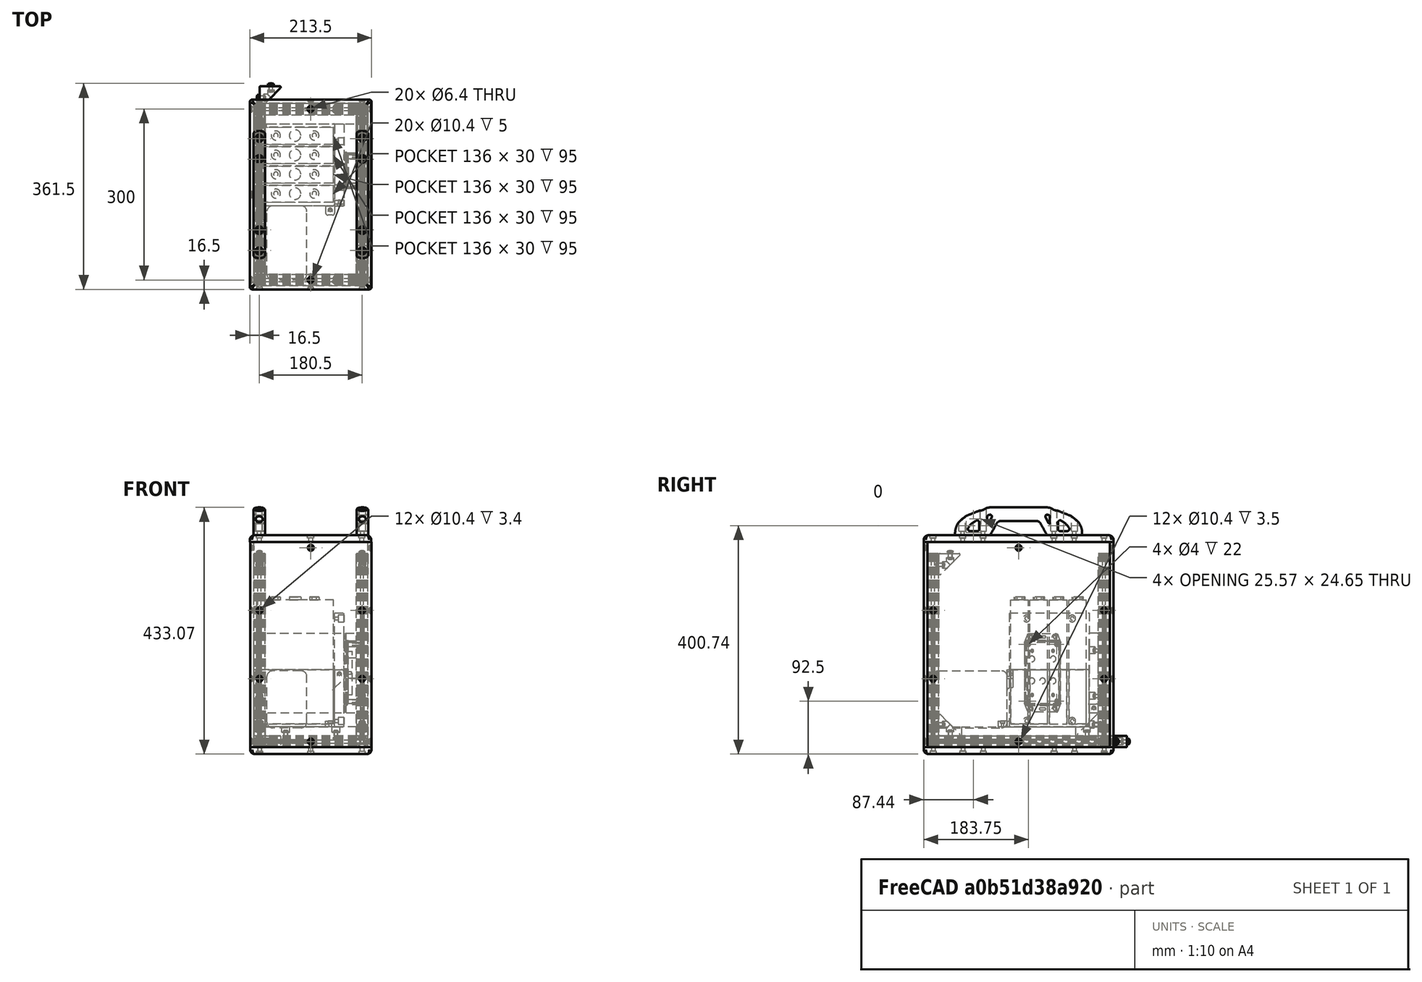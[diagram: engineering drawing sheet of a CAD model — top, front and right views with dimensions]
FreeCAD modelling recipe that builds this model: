
FCSTD DOCUMENT  (FreeCAD 0.17R9796 (Git))
Label: UPKframeNG2h
License: All rights reserved
LicenseURL: http://en.wikipedia.org/wiki/All_rights_reserved
objects: Part::Feature×72, Part::FeaturePython×24, Part::Compound×12, App::FeaturePython×8, App::Part×6, Part::Cylinder×5, Part::Box×4, Part::Cut×4, PartDesign::Body×2, PartDesign::Pocket×1, Part::Fillet×1, Part::MultiFuse×1
note: 127 computed .brp shape members not serialized (recipe doc carries the construction recipe); baked Part::Feature solids carry a one-line shape summary decoded from their .brp

FEATURE [Part::Feature] Pocket003001  label="tslot32con"
  Placement = pos=(0,10,10) rot=(1,0,0;1.5708rad)
  shape: bbox 20 x 320 x 20 mm, 150 faces (baked)
FEATURE [Part::Feature] Pocket003002  label="tslot16"
  Placement = pos=(10,0,10) rot=(0,1,0;1.5708rad)
  shape: bbox 160 x 20 x 20 mm, 94 faces (baked)
FEATURE [Part::Feature] Pocket003006  label="tslot16_001"
  Placement = pos=(10,-300,10) rot=(0,1,0;1.5708rad)
  shape: bbox 160 x 20 x 20 mm, 94 faces (baked)
FEATURE [Part::Feature] Pocket003007  label="tslot32con_001"
  Placement = pos=(180,-310,10) rot=(0,0.707107,0.707107;3.14159rad)
  shape: bbox 20 x 320 x 20 mm, 150 faces (baked)
FEATURE [Part::FeaturePython] Screw  label="M6x25-Screw"  # Fasteners workbench fastener (typed FeaturePython)
  Placement = pos=(-4,0,10) rot=(0,-1,0;1.5708rad)
  diameter = 7
  invert = false
  length = 6
  matchOuter = false
  offset = 0
  thread = false
  type = 15
FEATURE [Part::FeaturePython] Screw001  label="M6x25-Screw004"  # Fasteners workbench fastener (typed FeaturePython)
  Placement = pos=(-4,-300,10) rot=(0,-1,0;1.5708rad)
  diameter = 7
  invert = false
  length = 6
  matchOuter = false
  offset = 0
  thread = false
  type = 15
FEATURE [Part::FeaturePython] Screw002  label="M6x25-Screw005"  # Fasteners workbench fastener (typed FeaturePython)
  Placement = pos=(184,0,10) rot=(0,1,0;1.5708rad)
  diameter = 7
  invert = false
  length = 6
  matchOuter = false
  offset = 0
  thread = false
  type = 15
FEATURE [Part::FeaturePython] Screw004  label="M6x25-Screw006"  # Fasteners workbench fastener (typed FeaturePython)
  Placement = pos=(184,-300,10) rot=(0,1,0;1.5708rad)
  diameter = 7
  invert = false
  length = 6
  matchOuter = false
  offset = 0
  thread = false
  type = 15
FEATURE [App::Part] Part  label="lower_frame"
  Group = -> [Pocket003001,Pocket003002,Pocket003006,Pocket003007,Screw,Screw001,Screw002,Screw004]
  License = CC BY 3.0
  LicenseURL = http://creativecommons.org/licenses/by/3.0/
  Origin = -> PartOrigin
FEATURE [Part::Feature] Pocket003008  label="tslot32con001"
  Placement = pos=(0,10,10) rot=(1,0,0;1.5708rad)
  shape: bbox 20 x 320 x 20 mm, 150 faces (baked)
FEATURE [Part::Feature] Pocket003009  label="tslot041"
  Placement = pos=(10,0,10) rot=(0,1,0;1.5708rad)
  shape: bbox 160 x 20 x 20 mm, 94 faces (baked)
FEATURE [Part::Feature] Pocket003010  label="tslot16_002"
  Placement = pos=(10,-300,10) rot=(0,1,0;1.5708rad)
  shape: bbox 160 x 20 x 20 mm, 94 faces (baked)
FEATURE [Part::Feature] Pocket003011  label="tslot32con_002"
  Placement = pos=(180,-310,10) rot=(0,0.707107,0.707107;3.14159rad)
  shape: bbox 20 x 320 x 20 mm, 150 faces (baked)
FEATURE [Part::FeaturePython] Screw005  label="M6x25-Screw007"  # Fasteners workbench fastener (typed FeaturePython)
  Placement = pos=(-4,0,10) rot=(0,-1,0;1.5708rad)
  diameter = 7
  invert = false
  length = 6
  matchOuter = false
  offset = 0
  thread = false
  type = 15
FEATURE [Part::FeaturePython] Screw006  label="M6x25-Screw008"  # Fasteners workbench fastener (typed FeaturePython)
  Placement = pos=(-4,-300,10) rot=(0,-1,0;1.5708rad)
  diameter = 7
  invert = false
  length = 6
  matchOuter = false
  offset = 0
  thread = false
  type = 15
FEATURE [Part::FeaturePython] Screw007  label="M6x25-Screw009"  # Fasteners workbench fastener (typed FeaturePython)
  Placement = pos=(184,0,10) rot=(0,1,0;1.5708rad)
  diameter = 7
  invert = false
  length = 6
  matchOuter = false
  offset = 0
  thread = false
  type = 15
FEATURE [Part::FeaturePython] Screw008  label="M6x25-Screw010"  # Fasteners workbench fastener (typed FeaturePython)
  Placement = pos=(184,-300,10) rot=(0,1,0;1.5708rad)
  diameter = 7
  invert = false
  length = 6
  matchOuter = false
  offset = 0
  thread = false
  type = 15
FEATURE [App::Part] Part001  label="upper_frame"
  Group = -> [Pocket003008,Pocket003009,Pocket003010,Pocket003011,Screw005,Screw006,Screw007,Screw008]
  License = CC BY 3.0
  LicenseURL = http://creativecommons.org/licenses/by/3.0/
  Origin = -> PartOrigin001
  Placement = pos=(0,0,340) rot=(0,0,1;0rad)
FEATURE [Part::Feature] Fillet004001  label="Fillet005"
  shape: bbox 37.5 x 37.5 x 20 mm, 26 faces (baked)
FEATURE [Part::FeaturePython] Screw009  label="M6x12-Screw"  # Fasteners workbench fastener (typed FeaturePython)
  Placement = pos=(7,20,10) rot=(0,1,0;1.5708rad)
  diameter = 4
  invert = false
  length = 1
  matchOuter = false
  offset = 0
  thread = false
  type = 20
FEATURE [Part::Feature] Body001  label="m6nutplate"
  Placement = pos=(-1.5,15,5) rot=(0,-1,0;1.5708rad)
  shape: bbox 3 x 10 x 10 mm, 9 faces (baked)
FEATURE [App::Part] Part002  label="cornerstonescrewnut"
  License = CC BY 3.0
  LicenseURL = http://creativecommons.org/licenses/by/3.0/
  Origin = -> PartOrigin002
  Placement = pos=(10,-50,20) rot=(0,-1,0;1.5708rad)
FEATURE [Part::FeaturePython] Screw010  label="M6x12-Screw001"  # Fasteners workbench fastener (typed FeaturePython)
  Placement = pos=(20,33,10) rot=(1,0,0;1.5708rad)
  diameter = 4
  invert = false
  length = 1
  matchOuter = false
  offset = 0
  thread = false
  type = 20
FEATURE [Part::Feature] Body002  label="m6nutplate001"
  Placement = pos=(15,41.5,5) rot=(0.57735,0.57735,0.57735;4.18879rad)
  shape: bbox 10 x 3 x 10 mm, 9 faces (baked)
FEATURE [Part::Feature] Fillet004002  label="Fillet006"
  shape: bbox 37.5 x 37.5 x 20 mm, 26 faces (baked)
FEATURE [Part::FeaturePython] Screw011  label="M6x12-Screw002"  # Fasteners workbench fastener (typed FeaturePython)
  Placement = pos=(7,20,10) rot=(0,1,0;1.5708rad)
  diameter = 4
  invert = false
  length = 1
  matchOuter = false
  offset = 0
  thread = false
  type = 20
FEATURE [Part::Feature] Body003  label="m6nutplate002"
  Placement = pos=(-1.5,15,5) rot=(0,-1,0;1.5708rad)
  shape: bbox 3 x 10 x 10 mm, 9 faces (baked)
FEATURE [Part::FeaturePython] Screw012  label="M6x12-Screw003"  # Fasteners workbench fastener (typed FeaturePython)
  Placement = pos=(20,33,10) rot=(1,0,0;1.5708rad)
  diameter = 4
  invert = false
  length = 1
  matchOuter = false
  offset = 0
  thread = false
  type = 20
FEATURE [Part::Feature] Body004  label="m6nutplate003"
  Placement = pos=(15,41.5,5) rot=(0.57735,0.57735,0.57735;4.18879rad)
  shape: bbox 10 x 3 x 10 mm, 9 faces (baked)
FEATURE [App::Part] Part003  label="cornerstonescrewnut001"
  Group = -> [Body003,Screw011,Fillet004002,Screw012,Body004,PartOrigin002,Body001,Screw009,Fillet004001,Screw010,Body002,Part002]
  License = CC BY 3.0
  LicenseURL = http://creativecommons.org/licenses/by/3.0/
  Origin = -> PartOrigin003
  Placement = pos=(190,-50,20) rot=(0,-1,0;1.5708rad)
FEATURE [Part::Feature] Fillet004003  label="Fillet007"
  shape: bbox 37.5 x 37.5 x 20 mm, 26 faces (baked)
FEATURE [Part::FeaturePython] Screw013  label="M6x12-Screw004"  # Fasteners workbench fastener (typed FeaturePython)
  Placement = pos=(7,20,10) rot=(0,1,0;1.5708rad)
  diameter = 4
  invert = false
  length = 1
  matchOuter = false
  offset = 0
  thread = false
  type = 20
FEATURE [Part::Feature] Body005  label="m6nutplate004"
  Placement = pos=(-1.5,15,5) rot=(0,-1,0;1.5708rad)
  shape: bbox 3 x 10 x 10 mm, 9 faces (baked)
FEATURE [Part::FeaturePython] Screw014  label="M6x12-Screw005"  # Fasteners workbench fastener (typed FeaturePython)
  Placement = pos=(20,33,10) rot=(1,0,0;1.5708rad)
  diameter = 4
  invert = false
  length = 1
  matchOuter = false
  offset = 0
  thread = false
  type = 20
FEATURE [Part::Feature] Body006  label="m6nutplate005"
  Placement = pos=(15,41.5,5) rot=(0.57735,0.57735,0.57735;4.18879rad)
  shape: bbox 10 x 3 x 10 mm, 9 faces (baked)
FEATURE [App::Part] Part004  label="cornerstonescrewnut002"
  Group = -> [Body005,Screw013,Fillet004003,Screw014,Body006]
  License = CC BY 3.0
  LicenseURL = http://creativecommons.org/licenses/by/3.0/
  Origin = -> PartOrigin004
  Placement = pos=(-10,-50,340) rot=(0,1,0;1.5708rad)
FEATURE [Part::Feature] Fillet004004  label="Fillet008"
  shape: bbox 37.5 x 37.5 x 20 mm, 26 faces (baked)
FEATURE [Part::FeaturePython] Screw015  label="M6x12-Screw006"  # Fasteners workbench fastener (typed FeaturePython)
  Placement = pos=(7,20,10) rot=(0,1,0;1.5708rad)
  diameter = 4
  invert = false
  length = 1
  matchOuter = false
  offset = 0
  thread = false
  type = 20
FEATURE [Part::Feature] Body007  label="m6nutplate006"
  Placement = pos=(-1.5,15,5) rot=(0,-1,0;1.5708rad)
  shape: bbox 3 x 10 x 10 mm, 9 faces (baked)
FEATURE [Part::FeaturePython] Screw016  label="M6x12-Screw007"  # Fasteners workbench fastener (typed FeaturePython)
  Placement = pos=(20,33,10) rot=(1,0,0;1.5708rad)
  diameter = 4
  invert = false
  length = 1
  matchOuter = false
  offset = 0
  thread = false
  type = 20
FEATURE [Part::Feature] Body008  label="m6nutplate007"
  Placement = pos=(15,41.5,5) rot=(0.57735,0.57735,0.57735;4.18879rad)
  shape: bbox 10 x 3 x 10 mm, 9 faces (baked)
FEATURE [App::Part] Part005  label="cornerstonescrewnut003"
  Group = -> [Body007,Screw015,Fillet004004,Screw016,Body008]
  License = CC BY 3.0
  LicenseURL = http://creativecommons.org/licenses/by/3.0/
  Origin = -> PartOrigin005
  Placement = pos=(170,-50,340) rot=(0,1,0;1.5708rad)
FEATURE [Part::Feature] Body009001  label="m6nutplate010"
  Placement = pos=(-1.5,15,5) rot=(0,-1,0;1.5708rad)
  shape: bbox 3 x 10 x 10 mm, 9 faces (baked)
FEATURE [Part::Feature] Body010001  label="m6nutplate011"
  Placement = pos=(15,41.5,5) rot=(0.57735,0.57735,0.57735;4.18879rad)
  shape: bbox 10 x 3 x 10 mm, 9 faces (baked)
FEATURE [Part::Feature] Screw018001  label="M6x12-Screw010"
  Placement = pos=(20,33,10) rot=(1,0,0;1.5708rad)
  shape: bbox 10.5 x 15.3 x 10.5 mm, 15 faces (baked)
FEATURE [Part::Feature] Screw017001  label="M6x12-Screw011"
  Placement = pos=(7,20,10) rot=(0,1,0;1.5708rad)
  shape: bbox 15.3 x 10.5 x 10.5 mm, 15 faces (baked)
FEATURE [Part::Feature] Fillet004005001  label="Fillet010"
  shape: bbox 37.5 x 37.5 x 20 mm, 26 faces (baked)
FEATURE [Part::Compound] Compound
  Links = -> [Body009001,Fillet004005001,Screw017001,Body010001,Screw018001]
  Placement = pos=(10,-250,340) rot=(0.707107,0,-0.707107;3.14159rad)
FEATURE [Part::Feature] Body010002  label="m6nutplate012"
  Placement = pos=(-1.5,15,5) rot=(0,-1,0;1.5708rad)
  shape: bbox 3 x 10 x 10 mm, 9 faces (baked)
FEATURE [Part::Feature] Body010003  label="m6nutplate013"
  Placement = pos=(15,41.5,5) rot=(0.57735,0.57735,0.57735;4.18879rad)
  shape: bbox 10 x 3 x 10 mm, 9 faces (baked)
FEATURE [Part::Feature] Screw018002  label="M6x12-Screw012"
  Placement = pos=(20,33,10) rot=(1,0,0;1.5708rad)
  shape: bbox 10.5 x 15.3 x 10.5 mm, 15 faces (baked)
FEATURE [Part::Feature] Screw018003  label="M6x12-Screw013"
  Placement = pos=(7,20,10) rot=(0,1,0;1.5708rad)
  shape: bbox 15.3 x 10.5 x 10.5 mm, 15 faces (baked)
FEATURE [Part::Feature] Fillet004005002  label="Fillet011"
  shape: bbox 37.5 x 37.5 x 20 mm, 26 faces (baked)
FEATURE [Part::Compound] Compound001
  Links = -> [Body010002,Fillet004005002,Screw018003,Body010003,Screw018002]
  Placement = pos=(190,-250,340) rot=(0.707107,0,-0.707107;3.14159rad)
FEATURE [Part::Feature] Body010004  label="m6nutplate014"
  Placement = pos=(-1.5,15,5) rot=(0,-1,0;1.5708rad)
  shape: bbox 3 x 10 x 10 mm, 9 faces (baked)
FEATURE [Part::Feature] Body010005  label="m6nutplate015"
  Placement = pos=(15,41.5,5) rot=(0.57735,0.57735,0.57735;4.18879rad)
  shape: bbox 10 x 3 x 10 mm, 9 faces (baked)
FEATURE [Part::Feature] Screw018004  label="M6x12-Screw014"
  Placement = pos=(20,33,10) rot=(1,0,0;1.5708rad)
  shape: bbox 10.5 x 15.3 x 10.5 mm, 15 faces (baked)
FEATURE [Part::Feature] Screw018005  label="M6x12-Screw015"
  Placement = pos=(7,20,10) rot=(0,1,0;1.5708rad)
  shape: bbox 15.3 x 10.5 x 10.5 mm, 15 faces (baked)
FEATURE [Part::Feature] Fillet004005003  label="Fillet012"
  shape: bbox 37.5 x 37.5 x 20 mm, 26 faces (baked)
FEATURE [Part::Compound] Compound002
  Links = -> [Body010004,Fillet004005003,Screw018005,Body010005,Screw018004]
  Placement = pos=(10,-290,60) rot=(0.57735,0.57735,-0.57735;4.18879rad)
FEATURE [Part::Feature] Body010006  label="m6nutplate016"
  Placement = pos=(-1.5,15,5) rot=(0,-1,0;1.5708rad)
  shape: bbox 3 x 10 x 10 mm, 9 faces (baked)
FEATURE [Part::Feature] Body010007  label="m6nutplate017"
  Placement = pos=(15,41.5,5) rot=(0.57735,0.57735,0.57735;4.18879rad)
  shape: bbox 10 x 3 x 10 mm, 9 faces (baked)
FEATURE [Part::Feature] Screw018006  label="M6x12-Screw016"
  Placement = pos=(20,33,10) rot=(1,0,0;1.5708rad)
  shape: bbox 10.5 x 15.3 x 10.5 mm, 15 faces (baked)
FEATURE [Part::Feature] Screw018007  label="M6x12-Screw017"
  Placement = pos=(7,20,10) rot=(0,1,0;1.5708rad)
  shape: bbox 15.3 x 10.5 x 10.5 mm, 15 faces (baked)
FEATURE [Part::Feature] Fillet004005004  label="Fillet013"
  shape: bbox 37.5 x 37.5 x 20 mm, 26 faces (baked)
FEATURE [Part::Compound] Compound003
  Links = -> [Body010006,Fillet004005004,Screw018007,Body010007,Screw018006]
  Placement = pos=(190,-290,60) rot=(0.57735,0.57735,-0.57735;4.18879rad)
FEATURE [Part::Feature] Pocket001001  label="tslot32"
  Placement = pos=(0,0,20) rot=(0,0,1;0rad)
  shape: bbox 20 x 20 x 320 mm, 94 faces (baked)
FEATURE [Part::Feature] Body010008  label="m6nutplate018"
  Placement = pos=(-1.5,15,5) rot=(0,-1,0;1.5708rad)
  shape: bbox 3 x 10 x 10 mm, 9 faces (baked)
FEATURE [Part::Feature] Body010009  label="m6nutplate019"
  Placement = pos=(15,41.5,5) rot=(0.57735,0.57735,0.57735;4.18879rad)
  shape: bbox 10 x 3 x 10 mm, 9 faces (baked)
FEATURE [Part::Feature] Screw018008  label="M6x12-Screw018"
  Placement = pos=(20,33,10) rot=(1,0,0;1.5708rad)
  shape: bbox 10.5 x 15.3 x 10.5 mm, 15 faces (baked)
FEATURE [Part::Feature] Screw018009  label="M6x12-Screw019"
  Placement = pos=(7,20,10) rot=(0,1,0;1.5708rad)
  shape: bbox 15.3 x 10.5 x 10.5 mm, 15 faces (baked)
FEATURE [Part::Feature] Fillet004005005  label="Fillet014"
  shape: bbox 37.5 x 37.5 x 20 mm, 26 faces (baked)
FEATURE [Part::Compound] Compound004
  Links = -> [Body010008,Fillet004005005,Screw018009,Body010009,Screw018008]
  Placement = pos=(-10,-10,60) rot=(0.57735,-0.57735,0.57735;4.18879rad)
FEATURE [Part::Feature] Pocket003012  label="tslot32_001"
  Placement = pos=(0,-300,20) rot=(0,0,1;0rad)
  shape: bbox 20 x 20 x 320 mm, 94 faces (baked)
FEATURE [Part::Feature] Pocket003013  label="tslot32_002"
  Placement = pos=(180,0,20) rot=(0,0,1;0rad)
  shape: bbox 20 x 20 x 320 mm, 94 faces (baked)
FEATURE [Part::Feature] Pocket003014  label="tslot32_003"
  Placement = pos=(180,-300,20) rot=(0,0,1;0rad)
  shape: bbox 20 x 20 x 320 mm, 94 faces (baked)
FEATURE [PartDesign::Body] Body010027
FEATURE [Part::FeaturePython] Screw018021  label="M6x12-Screw032"  # Fasteners workbench fastener (typed FeaturePython)
  diameter = 4
  invert = false
  length = 1
  matchOuter = false
  offset = 0
  thread = false
  type = 20
FEATURE [Part::Feature] Body010028  label="m6nutplate032"
  Placement = pos=(5,-5,-8.39) rot=(0,1,0;3.14159rad)
  shape: bbox 10 x 10 x 3 mm, 9 faces (baked)
FEATURE [App::FeaturePython] circularEdgeConstraint009  # a2plus constraint (typed FeaturePython)
  Object1 = Screw
  Object2 = Body001
  SubElement1 = Edge7
  SubElement2 = Edge20
  Type = circularEdge
  directionConstraint = 1
  lockRotation = false
  offset = 0
FEATURE [Part::Compound] Compound017  label="nutplate12screw008"
  Links = -> [Screw018021,circularEdgeConstraint009,Body010028]
  Placement = pos=(10,30,6) rot=(0,0,1;0rad)
FEATURE [Part::FeaturePython] Screw018022  label="M6x12-Screw033"  # Fasteners workbench fastener (typed FeaturePython)
  diameter = 4
  invert = false
  length = 1
  matchOuter = false
  offset = 0
  thread = false
  type = 20
FEATURE [Part::Feature] Body010029  label="m6nutplate033"
  Placement = pos=(5,-5,-8.39) rot=(0,1,0;3.14159rad)
  shape: bbox 10 x 10 x 3 mm, 9 faces (baked)
FEATURE [App::FeaturePython] circularEdgeConstraint010  # a2plus constraint (typed FeaturePython)
  Object1 = Screw
  Object2 = Body001
  SubElement1 = Edge7
  SubElement2 = Edge20
  Type = circularEdge
  directionConstraint = 1
  lockRotation = false
  offset = 0
FEATURE [Part::Compound] Compound018  label="nutplate12screw009"
  Links = -> [Screw018022,circularEdgeConstraint010,Body010029]
  Placement = pos=(10,110,6) rot=(0,0,1;0rad)
FEATURE [Part::FeaturePython] Screw018023  label="M6x12-Screw034"  # Fasteners workbench fastener (typed FeaturePython)
  diameter = 4
  invert = false
  length = 1
  matchOuter = false
  offset = 0
  thread = false
  type = 20
FEATURE [Part::Feature] Body010030  label="m6nutplate034"
  Placement = pos=(5,-5,-8.39) rot=(0,1,0;3.14159rad)
  shape: bbox 10 x 10 x 3 mm, 9 faces (baked)
FEATURE [App::FeaturePython] circularEdgeConstraint011  # a2plus constraint (typed FeaturePython)
  Object1 = Screw
  Object2 = Body001
  SubElement1 = Edge7
  SubElement2 = Edge20
  Type = circularEdge
  directionConstraint = 1
  lockRotation = false
  offset = 0
FEATURE [Part::Compound] Compound019  label="nutplate12screw010"
  Links = -> [Screw018023,circularEdgeConstraint011,Body010030]
  Placement = pos=(190,110,6) rot=(0,0,1;0rad)
FEATURE [Part::FeaturePython] Screw018024  label="M6x12-Screw035"  # Fasteners workbench fastener (typed FeaturePython)
  diameter = 4
  invert = false
  length = 1
  matchOuter = false
  offset = 0
  thread = false
  type = 20
FEATURE [Part::Feature] Body010031  label="m6nutplate035"
  Placement = pos=(5,-5,-8.39) rot=(0,1,0;3.14159rad)
  shape: bbox 10 x 10 x 3 mm, 9 faces (baked)
FEATURE [App::FeaturePython] circularEdgeConstraint012  # a2plus constraint (typed FeaturePython)
  Object1 = Screw
  Object2 = Body001
  SubElement1 = Edge7
  SubElement2 = Edge20
  Type = circularEdge
  directionConstraint = 1
  lockRotation = false
  offset = 0
FEATURE [Part::Compound] Compound020  label="nutplate12screw011"
  Links = -> [Screw018024,circularEdgeConstraint012,Body010031]
  Placement = pos=(190,30,6) rot=(0,0,1;0rad)
FEATURE [Part::Compound] Compound021  label="front_plate"
  Links = -> [Body010027,Compound020,Compound019,Compound017,Compound018]
  Placement = pos=(-10,-10,60) rot=(1,0,0;1.5708rad)
FEATURE [Part::Compound] Compound016  label="bottom_plate"
  Placement = pos=(190,-310,20) rot=(0,0,1;1.5708rad)
FEATURE [PartDesign::Pocket] Pocket003019
  Length = 10
  Placement = pos=(130,-166,235) rot=(0,1,0;1.5708rad)
  Type = 0
FEATURE [Part::Box] Box003  label="MPPT"
  AttacherType = Attacher::AttachEngine3D
  Height = 100
  Length = 130
  Placement = pos=(290,128,10) rot=(0,0,1;0rad)
  Width = 70
FEATURE [Part::Fillet] Fillet007  label="MPPT               "
  Base = -> Box003
  Edges = 12 edges r=10: [Edge1,Edge2,Edge3,Edge4,Edge5,Edge6,Edge7,Edge8,Edge9,Edge10,Edge11,Edge12]
  Placement = pos=(211,-590,24) rot=(0,0,1;1.5708rad)
FEATURE [Part::Feature] Part__Feature1213  label="1591XXBF LID"
  Placement = pos=(153,-86,180) rot=(-0.57735,0.57735,0.57735;4.18879rad)
  shape: bbox 12.61 x 63.32 x 138 mm, 220 faces (baked)
FEATURE [Part::Feature] Part__Feature1212  label="1591XXB BOX"
  Placement = pos=(0,0,0) rot=(0,0.707107,0.707107;3.14159rad)
  shape: bbox 113.8 x 28.25 x 63.32 mm, 133 faces (baked)
FEATURE [Part::Cylinder] Cylinder  label="Zylinder"
  Angle = 360
  AttacherType = Attacher::AttachEngine3D
  Height = 60
  Placement = pos=(-14,48,18.6) rot=(1,0,0;1.5708rad)
  Radius = 5
FEATURE [Part::Cylinder] Cylinder001  label="Zylinder001"
  Angle = 360
  AttacherType = Attacher::AttachEngine3D
  Height = 60
  Placement = pos=(-14,48,0) rot=(1,0,0;1.5708rad)
  Radius = 5
FEATURE [Part::Cylinder] Cylinder002  label="Zylinder002"
  Angle = 360
  AttacherType = Attacher::AttachEngine3D
  Height = 60
  Placement = pos=(-14,48,-18.66) rot=(1,0,0;1.5708rad)
  Radius = 5
FEATURE [Part::Cylinder] Cylinder003  label="Zylinder003"
  Angle = 360
  AttacherType = Attacher::AttachEngine3D
  Height = 60
  Placement = pos=(24.49,48,18.6) rot=(1,0,0;1.5708rad)
  Radius = 5
FEATURE [Part::Cylinder] Cylinder004  label="Zylinder004"
  Angle = 360
  AttacherType = Attacher::AttachEngine3D
  Height = 60
  Placement = pos=(24.49,48,-18.66) rot=(1,0,0;1.5708rad)
  Radius = 5
FEATURE [Part::MultiFuse] Fusion
  Shapes = -> [Cylinder,Cylinder004,Cylinder003,Cylinder002,Cylinder001]
FEATURE [Part::Cut] Cut
  Base = -> Part__Feature1212
  Tool = -> Fusion
FEATURE [Part::Box] Box002  label="Würfel002"
  AttacherType = Attacher::AttachEngine3D
  Height = 10
  Length = 76
  Placement = pos=(-38,16,-36) rot=(0,0,1;0rad)
  Width = 12.6
FEATURE [Part::Cut] Cut001
  Base = -> Cut
  Tool = -> Box002
FEATURE [Part::Box] Box004  label="Würfel003"
  AttacherType = Attacher::AttachEngine3D
  Height = 10
  Length = 36
  Placement = pos=(-10,9,24) rot=(0,0,1;0rad)
  Width = 20
FEATURE [Part::Cut] Cut002
  Base = -> Cut001
  Tool = -> Box004
FEATURE [Part::Box] Box  label="Würfel"
  AttacherType = Attacher::AttachEngine3D
  Height = 20
  Length = 10
  Placement = pos=(49,23,-6) rot=(0,0,1;0rad)
  Width = 6
FEATURE [Part::Cut] Cut003  label="bms-cover"
  Base = -> Cut002
  Placement = pos=(179,-108,130.5) rot=(0.57735,-0.57735,0.57735;2.0944rad)
  Tool = -> Box
FEATURE [PartDesign::Body] Body010032
FEATURE [Part::FeaturePython] Screw018025  label="M6x12-Screw036"  # Fasteners workbench fastener (typed FeaturePython)
  diameter = 4
  invert = false
  length = 1
  matchOuter = false
  offset = 0
  thread = false
  type = 20
FEATURE [App::FeaturePython] circularEdgeConstraint013  # a2plus constraint (typed FeaturePython)
  Object1 = Screw
  Object2 = Body001
  SubElement1 = Edge7
  SubElement2 = Edge20
  Type = circularEdge
  directionConstraint = 1
  lockRotation = false
  offset = 0
FEATURE [Part::FeaturePython] Screw018026  label="M6x12-Screw037"  # Fasteners workbench fastener (typed FeaturePython)
  diameter = 4
  invert = false
  length = 1
  matchOuter = false
  offset = 0
  thread = false
  type = 20
FEATURE [Part::Feature] Body010034  label="m6nutplate037"
  Placement = pos=(5,-5,-8.39) rot=(0,1,0;3.14159rad)
  shape: bbox 10 x 10 x 3 mm, 9 faces (baked)
FEATURE [App::FeaturePython] circularEdgeConstraint014  # a2plus constraint (typed FeaturePython)
  Object1 = Screw
  Object2 = Body001
  SubElement1 = Edge7
  SubElement2 = Edge20
  Type = circularEdge
  directionConstraint = 1
  lockRotation = false
  offset = 0
FEATURE [Part::FeaturePython] Screw018027  label="M6x12-Screw038"  # Fasteners workbench fastener (typed FeaturePython)
  diameter = 4
  invert = false
  length = 1
  matchOuter = false
  offset = 0
  thread = false
  type = 20
FEATURE [Part::Feature] Body010035  label="m6nutplate038"
  Placement = pos=(5,-5,-8.39) rot=(0,1,0;3.14159rad)
  shape: bbox 10 x 10 x 3 mm, 9 faces (baked)
FEATURE [App::FeaturePython] circularEdgeConstraint015  # a2plus constraint (typed FeaturePython)
  Object1 = Screw
  Object2 = Body001
  SubElement1 = Edge7
  SubElement2 = Edge20
  Type = circularEdge
  directionConstraint = 1
  lockRotation = false
  offset = 0
FEATURE [Part::FeaturePython] Screw018028  label="M6x12-Screw039"  # Fasteners workbench fastener (typed FeaturePython)
  diameter = 4
  invert = false
  length = 1
  matchOuter = false
  offset = 0
  thread = false
  type = 20
FEATURE [Part::Feature] Body010036  label="m6nutplate039"
  Placement = pos=(5,-5,-8.39) rot=(0,1,0;3.14159rad)
  shape: bbox 10 x 10 x 3 mm, 9 faces (baked)
FEATURE [App::FeaturePython] circularEdgeConstraint016  # a2plus constraint (typed FeaturePython)
  Object1 = Screw
  Object2 = Body001
  SubElement1 = Edge7
  SubElement2 = Edge20
  Type = circularEdge
  directionConstraint = 1
  lockRotation = false
  offset = 0
FEATURE [Part::Compound] Compound026  label="bmsmounting_plate"
  Links = -> [Body010032]
  Placement = pos=(132,-26,36) rot=(0.707107,0,0.707107;3.14159rad)
FEATURE [Part::Feature] Body010037  label="batterymount"
  Placement = pos=(-10,-170,36) rot=(0,0,1;0rad)
  shape: bbox 158 x 176 x 100 mm, 72 faces (baked)
FEATURE [Part::Feature] Body010033  label="m6nutplate036"
  Placement = pos=(5,-5,-8.39) rot=(0,1,0;3.14159rad)
  shape: bbox 10 x 10 x 3 mm, 9 faces (baked)
FEATURE [Part::Feature] Body010038  label="cam72"
  Placement = pos=(130,-62,41) rot=(0,0,1;1.5708rad)
  shape: bbox 135.1 x 31 x 222.5 mm, 16 faces (baked)
FEATURE [Part::Feature] Body010039  label="cam72_001"
  Placement = pos=(130,-96,41) rot=(0,0,1;1.5708rad)
  shape: bbox 135.1 x 31 x 222.5 mm, 16 faces (baked)
FEATURE [Part::Feature] Body010040  label="cam72_002"
  Placement = pos=(130,-130,41) rot=(0,0,1;1.5708rad)
  shape: bbox 135.1 x 31 x 222.5 mm, 16 faces (baked)
FEATURE [Part::Feature] Body010041  label="cam72_003"
  Placement = pos=(130,-164,41) rot=(0,0,1;1.5708rad)
  shape: bbox 135.1 x 31 x 222.5 mm, 16 faces (baked)
FEATURE [Part::Feature] Body010042  label="backCover"
  Placement = pos=(-16.5,-310,0) rot=(1,0,0;1.5708rad)
  shape: bbox 213 x 6.5 x 360 mm, 26 faces (baked)
FEATURE [Part::Feature] Body010043  label="frontCover"
  Placement = pos=(196.5,10,0) rot=(0,0.707107,0.707107;3.14159rad)
  shape: bbox 213 x 6.5 x 360 mm, 26 faces (baked)
FEATURE [Part::Feature] Body010044  label="topCover"
  Placement = pos=(-17,-316.5,360) rot=(0,0,1;0rad)
  shape: bbox 213 x 333 x 12 mm, 48 faces (baked)
FEATURE [Part::Feature] Body010045  label="bottomCover"
  Placement = pos=(196.5,-316.5,0) rot=(0,1,0;3.14159rad)
  shape: bbox 213 x 333 x 12 mm, 48 faces (baked)
FEATURE [Part::Feature] Pocket003020  label="sideCover"
  Placement = pos=(190,-310,0) rot=(0.57735,0.57735,0.57735;2.0944rad)
  shape: bbox 6.5 x 320 x 360 mm, 24 faces (baked)
FEATURE [Part::Feature] Pocket003021  label="sideCover001"
  Placement = pos=(-10,10,0) rot=(-0.57735,0.57735,0.57735;4.18879rad)
  shape: bbox 6.5 x 320 x 360 mm, 24 faces (baked)
FEATURE [Part::Feature] Cut007001  label="handle"
  Placement = pos=(7,-150,372) rot=(0.57735,-0.57735,-0.57735;2.0944rad)
  shape: bbox 20 x 223 x 50.93 mm, 233 faces (baked)
FEATURE [Part::Feature] Cut007002  label="handle001"
  Placement = pos=(188,-150,372) rot=(0.57735,-0.57735,-0.57735;2.0944rad)
  shape: bbox 20 x 223 x 50.93 mm, 233 faces (baked)
